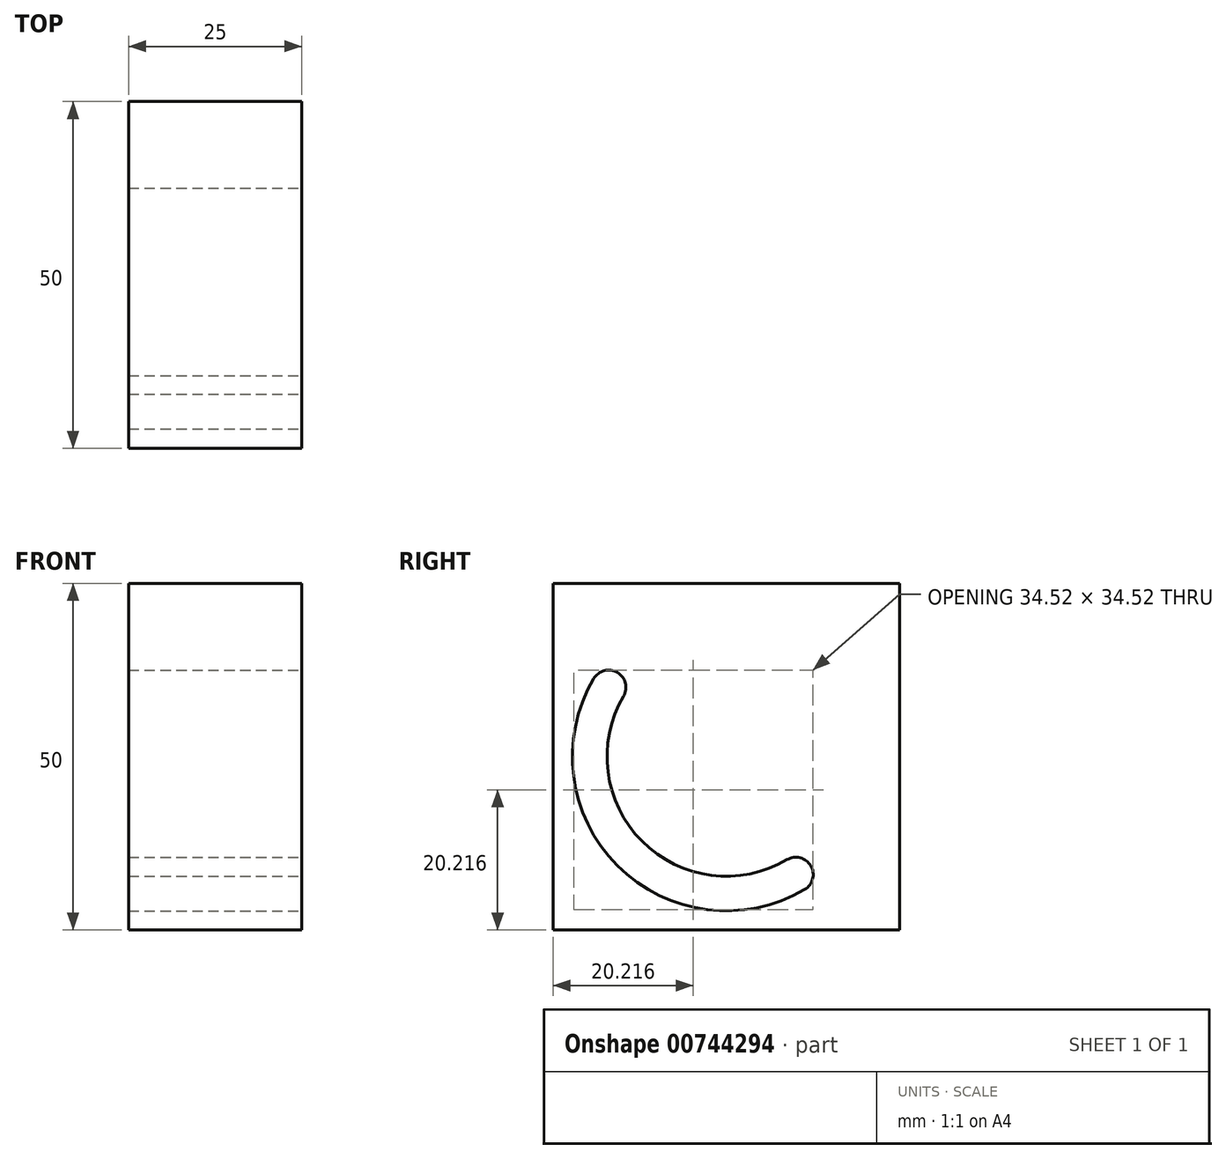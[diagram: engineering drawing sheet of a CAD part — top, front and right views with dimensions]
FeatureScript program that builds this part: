
annotation { "Feature Type Name" : "Feature", "Feature Type Description" : "" }
export const myFeature = defineFeature(function(context is Context, id is Id, definition is map)
    precondition{}
    {
        {
            var Q0;
            Q0=qCreatedBy(makeId("Right.planeOp"),FACE);
            var sketch = newSketch(context, id + "F0", { "sketchPlane" : qUnion([Q0])});
            skLineSegment(sketch, "E0.bottom", {"start": v(-25, 25) * mm, "end": v(25, 25) * mm});
            skLineSegment(sketch, "E0.top", {"start": v(-25, -25) * mm, "end": v(25, -25) * mm});
            skLineSegment(sketch, "E0.left", {"start": v(-25, 25) * mm, "end": v(-25, -25) * mm});
            skLineSegment(sketch, "E0.right", {"start": v(25, 25) * mm, "end": v(25, -25) * mm});
            skSolve(sketch);
        }
        {
            var Q0;
            Q0=makeQuery(id+"F0.imprint","IMPRINT",FACE,{"disambiguationData":[TD([[makeQuery(id+"F0.imprint","IMPRINT",EDGE,{"derivedFrom":sQuery(id+"F0.wireOp",EDGE,"E0.bottom")}),-1.0]])]});
            extrude(context, id + "F1", {"entities" : qUnion([Q0]), "depth" : 25 * mm, "offsetDistance" : 25 * mm});
        }
        {
            var Q0;
            Q0=makeQuery(id+"F1.opExtrude","CAP_FACE",FACE,{"disambiguationData":[OSD([sQuery(id+"F0.wireOp",EDGE,"E0.bottom"),sQuery(id+"F0.wireOp",EDGE,"E0.top"),sQuery(id+"F0.wireOp",EDGE,"E0.left"),sQuery(id+"F0.wireOp",EDGE,"E0.right")])],"isStart":false});
            var sketch = newSketch(context, id + "F2", { "sketchPlane" : qUnion([Q0])});
            skArc(sketch, "E1", {"start": v(-14.85, 8.73) * mm, "mid": v(-12.18, -12.18) * mm, "end": v(8.73, -14.85) * mm});
            skArc(sketch, "E2.0", {"start": v(-19.15, 11.27) * mm, "mid": v(-15.71, -15.71) * mm, "end": v(11.27, -19.15) * mm});
            skArc(sketch, "E3", {"start": v(-14.85, 8.73) * mm, "mid": v(-15.73, 12.15) * mm, "end": v(-19.15, 11.27) * mm});
            skArc(sketch, "E4", {"start": v(11.27, -19.15) * mm, "mid": v(12.15, -15.73) * mm, "end": v(8.73, -14.85) * mm});
            skSolve(sketch);
        }
        {
            var Q0;
            Q0 = qSketchRegion(id + "F2", true);
            extrude(context, id + "F3", {"entities" : qUnion([Q0]), "operationType" : NewBodyOperationType.REMOVE, "oppositeDirection" : true, "depth" : 25 * mm, "offsetDistance" : 25 * mm});
        }
    });
